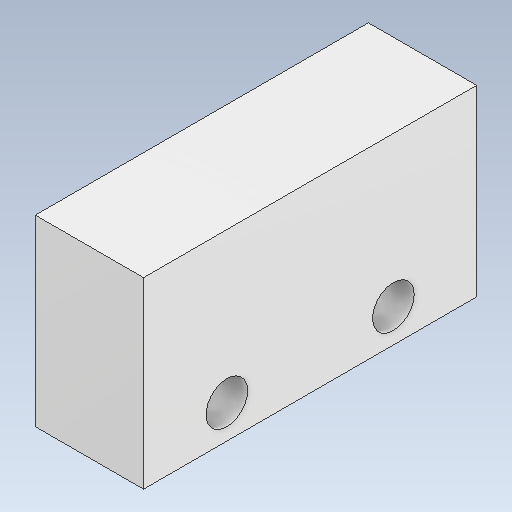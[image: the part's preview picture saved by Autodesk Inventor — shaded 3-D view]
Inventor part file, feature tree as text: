
AUTODESK INVENTOR PART (.ipt)
format: ipt  version: 2020 (Build 240168000, 168)  size: 107,520 bytes
history: native  units: mm
features: extrude x2, sketch x2, other x1
ambient origin geometry x8: Origin, YZ Plane, XZ Plane, XY Plane, X Axis, Y Axis, Z Axis, Center Point
bodies: Body1 (feature_tree)
feature tree (5):
  other  "Bryła1"
  extrude  "Wyciągnięcie proste1"  Depth=20.0mm
  extrude  "Wyciągnięcie proste2"  Depth=11.0mm
  sketch  "Szkic1"
  sketch  "Szkic2"
